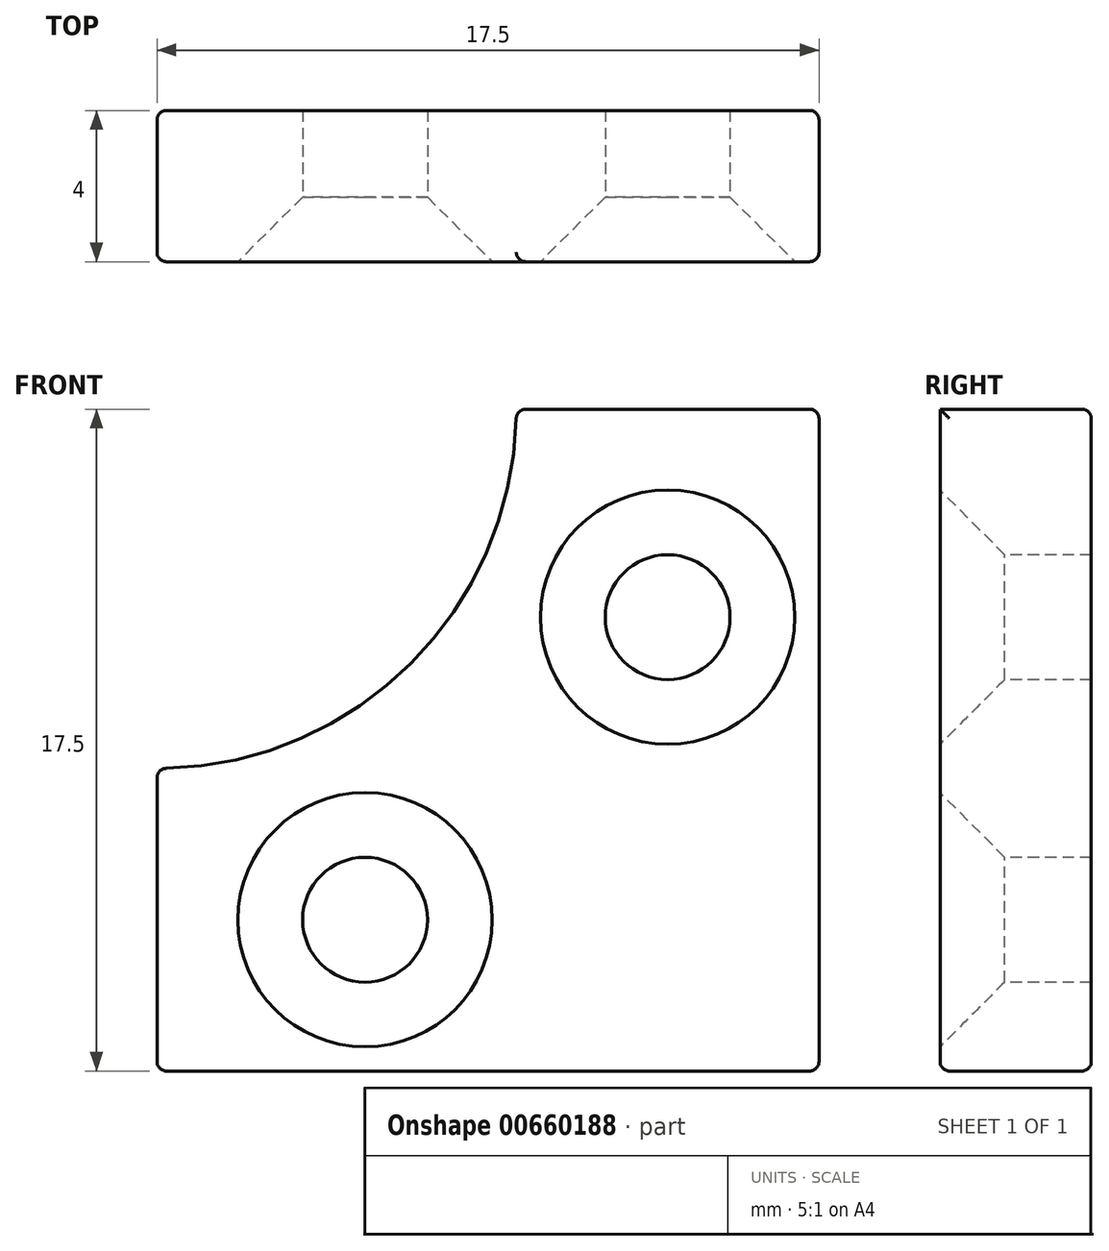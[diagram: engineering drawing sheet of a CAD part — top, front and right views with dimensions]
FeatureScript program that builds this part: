
annotation { "Feature Type Name" : "Feature", "Feature Type Description" : "" }
export const myFeature = defineFeature(function(context is Context, id is Id, definition is map)
    precondition{}
    {
        {
            var Q0;
            Q0=qCreatedBy(makeId("Front.planeOp"),FACE);
            var sketch = newSketch(context, id + "F0", { "sketchPlane" : qUnion([Q0])});
            skArc(sketch, "E0", {"start": v(0, -9.5) * mm, "mid": v(6.72, -6.72) * mm, "end": v(9.5, 0) * mm});
            skLineSegment(sketch, "E1", {"start": v(9.5, 0) * mm, "end": v(17.5, 0) * mm});
            skLineSegment(sketch, "E2", {"start": v(17.5, 0) * mm, "end": v(17.5, -17.5) * mm});
            skLineSegment(sketch, "E3", {"start": v(17.5, -17.5) * mm, "end": v(0, -17.5) * mm});
            skLineSegment(sketch, "E4", {"start": v(0, -17.5) * mm, "end": v(0, -9.5) * mm});
            skPoint(sketch, "E5", {"position": v(13.5, -13.5) * mm});
            skPoint(sketch, "E5.positionSnap0", {"position": v(0, -13.5) * mm});
            skPoint(sketch, "E5.positionSnap1", {"position": v(13.5, 0) * mm});
            skPoint(sketch, "E6", {"position": v(13.5, -4) * mm});
            skSolve(sketch);
        }
        {
            var Q0;
            Q0=makeQuery(id+"F0.imprint","IMPRINT",FACE,{"disambiguationData":[TD([[makeQuery(id+"F0.imprint","IMPRINT",EDGE,{"derivedFrom":sQuery(id+"F0.wireOp",EDGE,"E0")}),-1.0]])]});
            extrude(context, id + "F1", {"entities" : qUnion([Q0]), "depth" : 4 * mm, "offsetDistance" : 25 * mm});
        }
        {
            var Q0;
            Q0=makeQuery(id+"F1.opExtrude","CAP_FACE",FACE,{"disambiguationData":[OSD([sQuery(id+"F0.wireOp",EDGE,"E0"),sQuery(id+"F0.wireOp",EDGE,"E1"),sQuery(id+"F0.wireOp",EDGE,"E2"),sQuery(id+"F0.wireOp",EDGE,"E3"),sQuery(id+"F0.wireOp",EDGE,"E4")])],"isStart":false});
            var sketch = newSketch(context, id + "F2", { "sketchPlane" : qUnion([Q0])});
            skPoint(sketch, "E7.positionSnap0", {"position": v(0, -13.5) * mm});
            skPoint(sketch, "E7.positionSnap1", {"position": v(13.5, 0) * mm});
            skPoint(sketch, "E8", {"position": v(13.5, -5.5) * mm});
            skPoint(sketch, "E9", {"position": v(5.5, -13.5) * mm});
            skSolve(sketch);
        }
        {
            var Q0;
            Q0=sQuery(id+"F2.wireOp",VERTEX,"E8");
            var Q1;
            Q1=sQuery(id+"F2.wireOp",VERTEX,"E9");
            var Q2;
            Q2=makeQuery(id+"F1.opExtrude","SWEPT_BODY",BODY,{"disambiguationData":[OSD([sQuery(id+"F0.wireOp",EDGE,"E0"),sQuery(id+"F0.wireOp",EDGE,"E1"),sQuery(id+"F0.wireOp",EDGE,"E2"),sQuery(id+"F0.wireOp",EDGE,"E3"),sQuery(id+"F0.wireOp",EDGE,"E4")])]});
            hole(context, id + "F3", {"style" : HoleStyle.C_SINK, "endStyle" : HoleEndStyle.THROUGH, "standardTappedOrClearance" : lookupTablePath({ "standard" : "ISO", "fit" : "Normal", "size" : "M3", "type" : "Clearance" }), "standardBlindInLast" : lookupTablePath({ "fit" : "Standard", "standard" : "ISO", "size" : "M3", "type" : "Clearance" }), "holeDiameter" : 3.3 * mm, "cSinkDiameter" : 6.72 * mm, "cSinkAngle" : 90 * degree, "majorDiameter" : 5 * mm, "isTappedThrough" : true, "tappedDepth" : 19 * mm, "tapClearance" : 3, "startFromSketch" : true, "locations" : qUnion([Q0, Q1]), "scope" : qUnion([Q2])});
        }
        {
            var Q0;
            Q0=makeQuery(id+"F3.hole-1.boolean.opBoolean","INTERSECT",EDGE,{"derivedFrom":[makeQuery(id+"F1.opExtrude","CAP_FACE",FACE,{"disambiguationData":[OSD([sQuery(id+"F0.wireOp",EDGE,"E0"),sQuery(id+"F0.wireOp",EDGE,"E1"),sQuery(id+"F0.wireOp",EDGE,"E2"),sQuery(id+"F0.wireOp",EDGE,"E3"),sQuery(id+"F0.wireOp",EDGE,"E4")])],"isStart":true}),makeQuery(id+"F3.hole-1.opRevolve","SWEPT_FACE",FACE,{"disambiguationData":[OSD([sQuery(id+"F3.hole-1.sketch.wireOp",EDGE,"core_line_2")])]})]});
            var Q1;
            Q1=makeQuery(id+"F1.opExtrude","SWEPT_FACE",FACE,{"disambiguationData":[OSD([sQuery(id+"F0.wireOp",EDGE,"E0")])]});
            var Q2;
            Q2=makeQuery(id+"F1.opExtrude","CAP_EDGE",EDGE,{"disambiguationData":[OSD([sQuery(id+"F0.wireOp",EDGE,"E1")])],"isStart":true});
            var Q3;
            Q3=makeQuery(id+"F1.opExtrude","SWEPT_FACE",FACE,{"disambiguationData":[OSD([sQuery(id+"F0.wireOp",EDGE,"E4")])]});
            var Q4;
            Q4=makeQuery(id+"F1.opExtrude","SWEPT_FACE",FACE,{"disambiguationData":[OSD([sQuery(id+"F0.wireOp",EDGE,"E2")])]});
            var Q5;
            Q5=makeQuery(id+"F1.opExtrude","SWEPT_FACE",FACE,{"disambiguationData":[OSD([sQuery(id+"F0.wireOp",EDGE,"E3")])]});
            fillet(context, id + "F4", {"entities" : qUnion([Q0, Q1, Q2, Q3, Q4, Q5]), "radius" : .25 * mm, "tangentPropagation" : true, "allowEdgeOverflow" : false});
        }
    });
